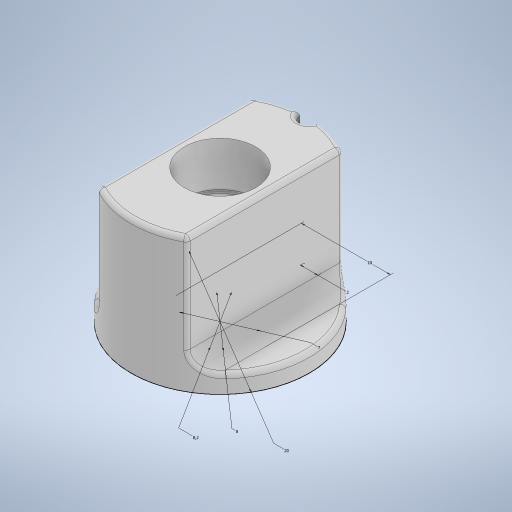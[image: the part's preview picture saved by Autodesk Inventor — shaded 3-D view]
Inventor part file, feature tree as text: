
AUTODESK INVENTOR PART (.ipt)
format: ipt  version: 2024 (Build 280153000, 153)  size: 397,312 bytes
history: native  units: mm
features: extrude x7, fillet x4, sketch x2, other x1
ambient origin geometry x8: Origin, YZ Plane, XZ Plane, XY Plane, X Axis, Y Axis, Z Axis, Center Point
bodies: Body1 (feature_tree)
feature tree (14):
  other  "Твердое тело1"
  sketch  "Эскиз1"
  extrude  "Выдавливание1"  Depth=6.15mm
  extrude  "Выдавливание2"  Depth=8.0mm
  fillet  "Сопряжение3"  Radius=20.0mm
  fillet  "Сопряжение7"  Radius=10.0mm
  fillet  "Сопряжение8"  Radius=2.0mm
  extrude  "Выдавливание7"  Depth=2.0mm TaperAngle=0.0deg
  extrude  "Выдавливание8"  Depth=15.0mm TaperAngle=0.0deg
  fillet  "Сопряжение12"  Radius=2.0mm
  extrude  "Выдавливание10"  Depth=7.0mm
  extrude  "Выдавливание11"  Depth=0.5mm
  extrude  "Выдавливание12"  Depth=0.5mm
  sketch  "Эскиз4"
